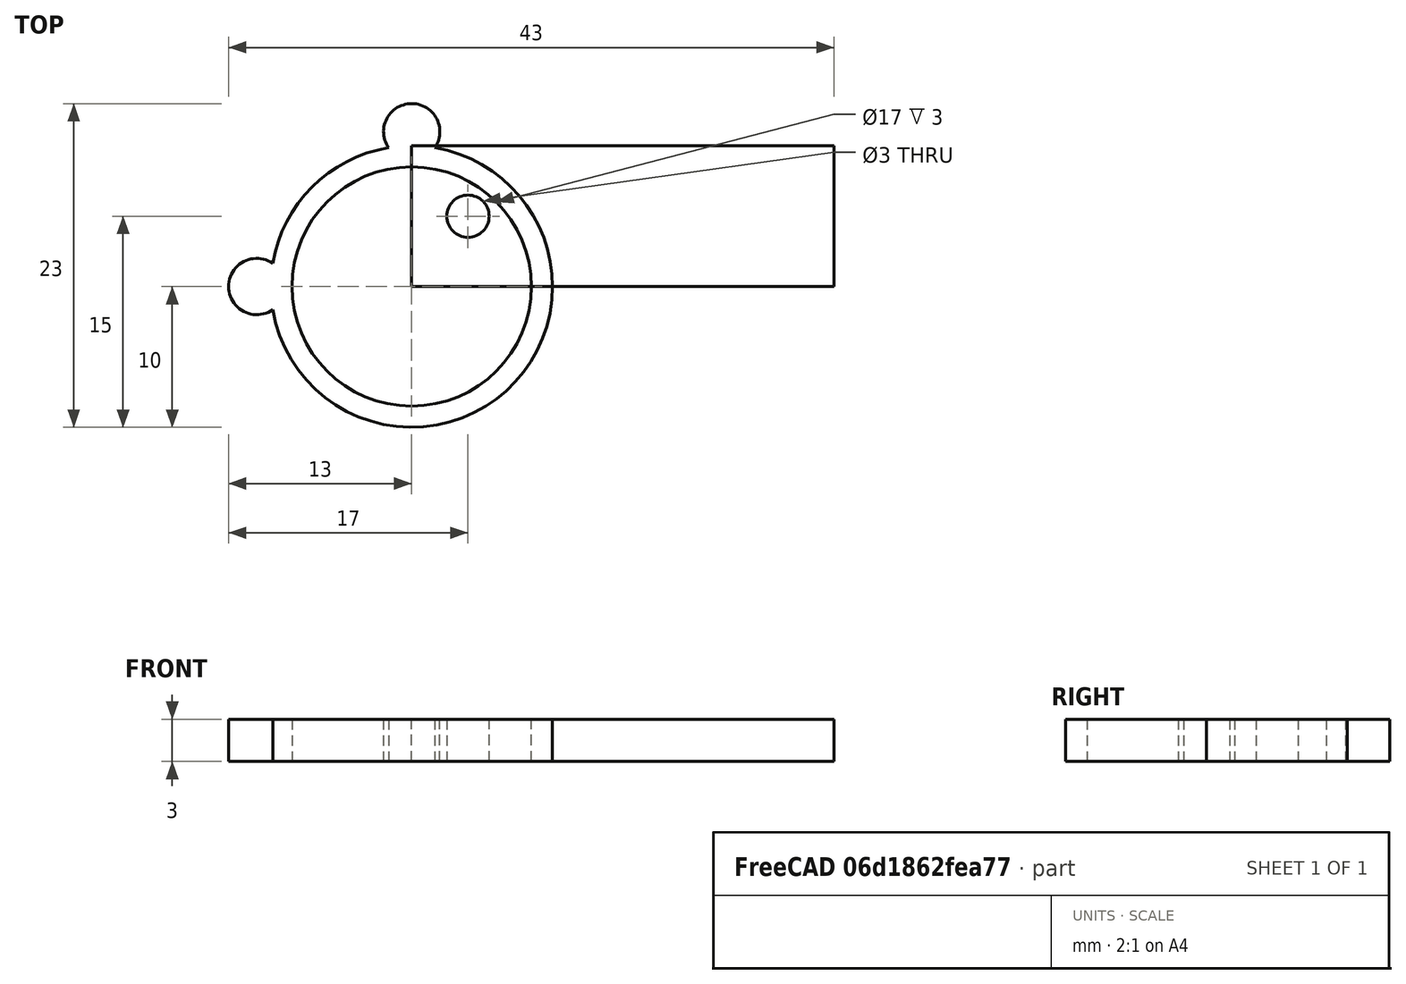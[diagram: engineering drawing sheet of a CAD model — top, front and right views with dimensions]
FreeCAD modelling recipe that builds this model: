
FCSTD DOCUMENT  (FreeCAD 1.0R38806 (Git))
Label: Unnamed1
License: All rights reserved
LicenseURL: https://en.wikipedia.org/wiki/All_rights_reserved
objects: Part::Cylinder×5, Part::Cut×2, Part::Box×1, Part::MultiFuse×1
note: 9 computed .brp shape members not serialized (recipe doc carries the construction recipe); baked Part::Feature solids carry a one-line shape summary decoded from their .brp

FEATURE [Part::Box] Box  label="Cube"
  AttacherType = Attacher::AttachEngine3D
  Height = 3
  Length = 30
  Width = 10
FEATURE [Part::Cylinder] Cylinder
  Angle = 360
  AttacherType = Attacher::AttachEngine3D
  FirstAngle = 0
  Height = 10
  Placement = pos=(4,5,0) rot=(0,0,1;0rad)
  Radius = 1.5
  SecondAngle = 0
FEATURE [Part::Cut] Cut
  Base = -> Box
  Tool = -> Cylinder
FEATURE [Part::Cylinder] Cylinder001
  Angle = 360
  AttacherType = Attacher::AttachEngine3D
  FirstAngle = 0
  Height = 3
  Radius = 10
  SecondAngle = 0
FEATURE [Part::Cylinder] Cylinder002
  Angle = 360
  AttacherType = Attacher::AttachEngine3D
  FirstAngle = 0
  Height = 10
  Radius = 8.5
  SecondAngle = 0
FEATURE [Part::Cut] Cut001
  Base = -> Cylinder001
  Tool = -> Cylinder002
FEATURE [Part::Cylinder] Cylinder003
  Angle = 360
  AttacherType = Attacher::AttachEngine3D
  FirstAngle = 0
  Height = 3
  Placement = pos=(0,11,0) rot=(0,0,1;0rad)
  Radius = 2
  SecondAngle = 0
FEATURE [Part::Cylinder] Cylinder004
  Angle = 360
  AttacherType = Attacher::AttachEngine3D
  FirstAngle = 0
  Height = 3
  Placement = pos=(-11,0,0) rot=(0,0,1;0rad)
  Radius = 2
  SecondAngle = 0
FEATURE [Part::MultiFuse] Fusion  label="Anillo"
  Shapes = -> [Cut001,Cylinder004,Cylinder003]
